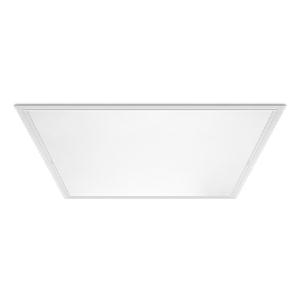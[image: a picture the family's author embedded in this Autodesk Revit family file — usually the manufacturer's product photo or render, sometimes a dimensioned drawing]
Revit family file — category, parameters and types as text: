
# Revit family: 3f_filippi_-_l_340_luce_diffusa_vs_ip65v_3f_filippi_-_23907_-_l_340_38w-840_dali_vs_ip65v_621x621
name_source: partatom
category: Lighting Fixtures
units: mm (PartAtom-declared; Revit-internal decimal feet)

## family parameters
Cut with Voids When Loaded = No
Host = Face
Light Source = No
Part Type = Normal
Room Calculation Point = No
Round Connector Dimension = Use Diameter
Shared = No

## types (1)
- 3F Filippi - L 340 Luce Diffusa VS IP65V (1 x LED, 5248 lm, 43 W, 4000 K)
    Apparent Load = 43 VA
    Approval mark = ENEC
    CIE Flux Codes = 61 89 98 100 100
    Color Rendering = 80
    Color Temperature = 4000 K
    Control Gear = Electronic transformer
    Default Elevation = 1800 mm
    Description = ILLUMINOTECHNICAL
Luminous efficiency 100% (DLOR 100%, ULOR 0%).
Initial luminous flux of the luminaire 5248 lm.
Direct symmetric distribution.
Installation Interdistance Transv.D = 1.17 x hu - Long.D = 1.14 x hu.
Average luminance <3000 cd/m² for radial angles >65°.
Tabular UGR (CIE 117 - 4H-8H; S=0.25H; 70/50/20): RUG 19 - 18.8.
Beam angle: 91° - 88°.
Luminous efficacy 122 lm/W.
Lifetime (L93/B10): 30000 h. (tq+25°C)
Lifetime (L90/B10): 50000 h. (tq+25°C)
Lifetime (L85/B10): 80000 h. (tq+25°C)
Lifetime (L80/B10): 100000 h. (tq+25°C)
Sudden decreased luminous flux after 50000 hours: 0% (C0).
Photobiological safety in compliance with IEC/TR 62778: RG0 risk exempt, (IEC 62471).
In compliance with IEC/EN 62722-2-1 - IEC/EN 62717 standards.

SOURCE
Squared LED module 38W/840.
Energy efficiency class (UE 2019/2020 - UE 2019/2015): C.
CIE 13.3 Colour rendering index: CRI >80 (R9 <50%).
IES TM-30 Fidelity Index: Rf = 84 Rg = 95.
CCT nominal colour temperature 4000 K.
Colour initial tolerance (MacAdam): SDCM 3.

MECHANICAL
Housing in hot-galvanised steel, painted in white polyester.
Perimetral frame in white polycarbonate.
VS moulded glass, anti-glare, tempered, non-combustible, thickness 4 mm.
Luminaire with limited surface temperature. - D - (EN 60598-2-24)
Dimensions: 621x621 mm, height 80 mm. Weight 6.62 kg.
IP65 protection degree for exposed part, IP40 for recessed part.
Mechanical strength to impacts IK08 (5 joule).
Glow-wire test resistance 960°C.

ELECTRICAL
Wiring on a separate unit.
Halogen Free DALI-2 DATI (Parts 251, 252, 253), PUSH-DIM, electronic wiring 230V-50/60Hz, power factor 0.95 at full load, THD <25%, constant output current, SELV, class II, 1 driver, 1 DALI addresse.
Power of the luminaire 43 W.
CE - IEC 60598-1 - EN 60598-1.
SAFE FLICKER: PstLM=<1 and SVM=<0.4 (IEC TR 61547-1 and IEC TR 63158), to ensure a more comfortable and safe light.
Luminaire compliant with EN 60598-2-22 for power supply from a centralised emergency system CPSS (Central Power Supply System), not incorporated in the luminaire - high risk areas excluded. The default power and flux are 100% in AC and 15% in DC.
Ambient temperature from 0°C to +40°C.
Temperature class T6 max 85°C.
Relative humidity UR: <85%.

INSTALLATION
Lay-in recessed fitting.
All accessories dedicated to this product are available on the Catalog and on our website www.3F-Filippi.com.

APPLICATIONS
In environments requiring protection and simplified cleaning.
Hospitals, pharmaceutical, chemical, aseptic laboratories, sterilised rooms.
Environments: with VDTs, meeting rooms, offices.
Environments: architectural, commercial, staterooms, banks.
Environments where demanding visual tasks are performed and soft diffuse light is required for optimal visual comfort and total shielding of the light source.

LIGHT MANAGEMENT
Recommended minimum setting: 10%.
The luminaire, equipped with (DALI-2 DATI) driver, can be controlled manually with 3F Easy Dim technology or automatically/manually with wired or wireless DALI/D2D control systems.
The D2D driver guarantees interoperability with other devices with the same certification by making the following information available:
Device Data (Part 251), Energy Report (Part 252), Diagnosis & Maintenance (Part 253).
In electrical systems without a regulation system (manual or automatic) and DALI bus, a suitable jumper must be made on the DA-DA terminals of the appliance.

WARNING
Luminaire designed for disposal/recycling at end-of-life.
Replaceable (LED only) light source by a professional. Replaceable control gear by a professional.
    Height = 0 mm  [stored 0 ft]
    Lamp = 1 x LED
    Lamp Light Flux = 5248 lm
    Lamp Power = 43 W
    Lamp count = 1
    Length = 621 mm
    Lifetime = 50000 h
    Luminous efficacy = 122 lm/W
    Manufacturer = 3F Filippi
    ModVariant = No
    Model = 3F Filippi - 23907 - L 340 38W-840 DALI VS IP65V 621x621
    Mounting Place = Ceiling
    Mounting Type = Recessed
    Number of Poles = 1
    OnlyDefault = Yes
    Power Factor = 1
    Product Name = 3F Filippi - L 340 Luce Diffusa VS IP65V
    Product group = recessed luminaire
    ProductGroupID = 4
    Protection Class = Protection class II
    Protection Degree = IP 40
    RLX_Detail_Level = 1
    RLX_Emergency_Light_Flux = 0 lm
    RLX_Emergency_Type = 0
    RLX_Emergency_Type_DB = No
    RlxData = <blob elided: 161557 chars, md5=2252ca87>
    Socket = socket
    Standby Power = 0 W
    System Light Flux = 5248 lm
    System Power = 43 W
    Type Comments = Product without accessories
    Type Image = 3ffilippi_l_340_luce_diffusa_vs.jpg
    URL = http://relux.com
    VarID = ---
    Voltage = 0 V
    Weight = 0.00 kg
    Width = 621 mm

note: [stored X ft] marks values corroborated as IEEE doubles in the binary element streams (Revit-internal decimal feet)

## geometry (parser evidence)
native form markers: Blend x4, Sweep x11
no freeform markers — native parametric forms only
